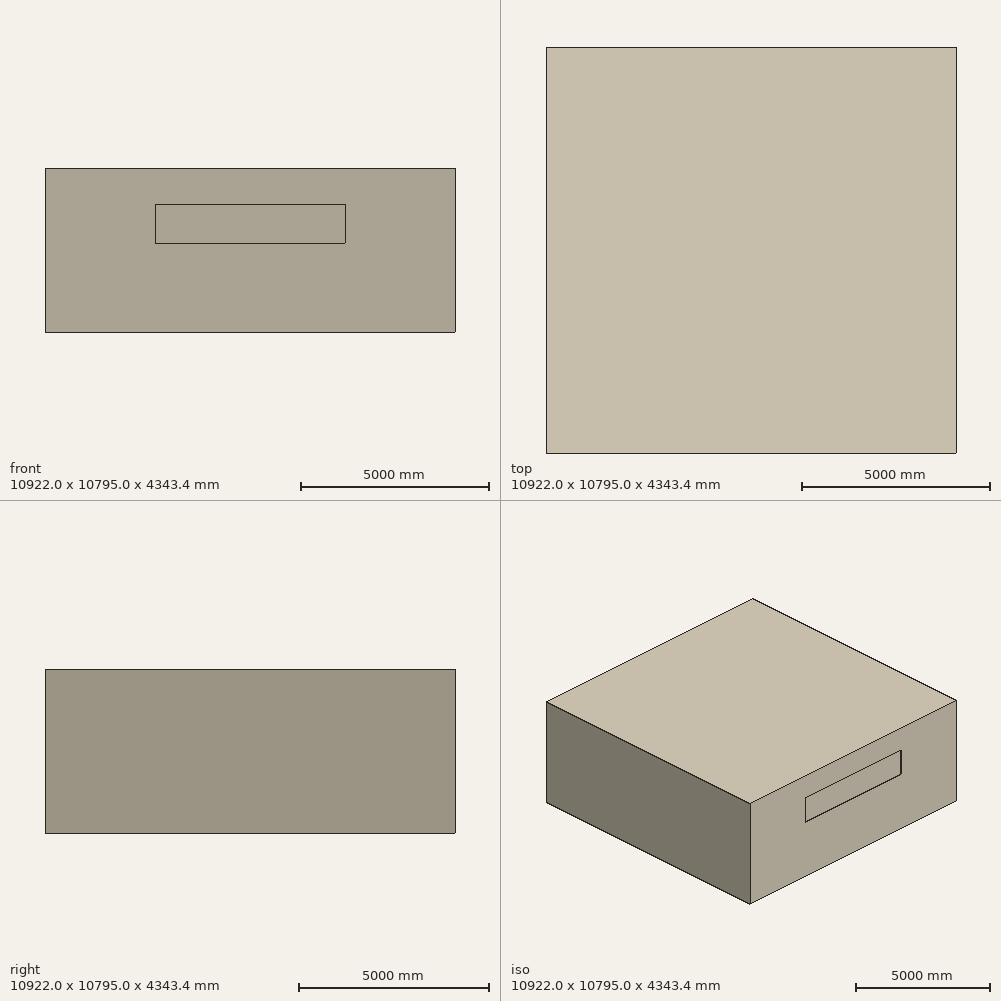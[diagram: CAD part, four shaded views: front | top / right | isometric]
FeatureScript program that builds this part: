
annotation { "Feature Type Name" : "Feature", "Feature Type Description" : "" }
export const myFeature = defineFeature(function(context is Context, id is Id, definition is map)
    precondition{}
    {
        {
            var Q0;
            Q0=qCreatedBy(makeId("Front.planeOp"),FACE);
            var sketch = newSketch(context, id + "F0", { "sketchPlane" : qUnion([Q0])});
            skLineSegment(sketch, "E0.bottom", {"start": v(-5461, -2171.7) * mm, "end": v(5461, -2171.7) * mm});
            skLineSegment(sketch, "E0.top", {"start": v(-5461, 2171.7) * mm, "end": v(5461, 2171.7) * mm});
            skLineSegment(sketch, "E0.left", {"start": v(-5461, -2171.7) * mm, "end": v(-5461, 2171.7) * mm});
            skLineSegment(sketch, "E0.right", {"start": v(5461, -2171.7) * mm, "end": v(5461, 2171.7) * mm});
            skPoint(sketch, "E0.middle", {"position": v(0, 0) * mm});
            skSolve(sketch);
        }
        {
            var Q0;
            Q0 = qSketchRegion(id + "F0", true);
            extrude(context, id + "F1", {"entities" : qUnion([Q0]), "depth" : 10795 * mm});
        }
        {
            var Q0;
            Q0=makeQuery(id+"F1.opExtrude","CAP_FACE",FACE,{"disambiguationData":[OSD([sQuery(id+"F0.wireOp",EDGE,"E0.bottom"),sQuery(id+"F0.wireOp",EDGE,"E0.top"),sQuery(id+"F0.wireOp",EDGE,"E0.left"),sQuery(id+"F0.wireOp",EDGE,"E0.right")])],"isStart":false});
            var sketch = newSketch(context, id + "F2", { "sketchPlane" : qUnion([Q0])});
            skLineSegment(sketch, "E1.bottom", {"start": v(-2535.01, 1221.87) * mm, "end": v(2535.01, 1221.87) * mm});
            skLineSegment(sketch, "E1.top", {"start": v(-2535.01, 179.2) * mm, "end": v(2535.01, 179.2) * mm});
            skLineSegment(sketch, "E1.left", {"start": v(-2535.01, 1221.87) * mm, "end": v(-2535.01, 179.2) * mm});
            skLineSegment(sketch, "E1.right", {"start": v(2535.01, 1221.87) * mm, "end": v(2535.01, 179.2) * mm});
            skPoint(sketch, "E1.middle", {"position": v(0, 700.54) * mm});
            skPoint(sketch, "E1.middle.positionSnap0", {"position": v(0, 2171.7) * mm});
            skPoint(sketch, "E1.centerSnap0", {"position": v(0, 2171.7) * mm});
            skSolve(sketch);
        }
        {
            var Q0;
            Q0 = qSketchRegion(id + "F2", true);
            extrude(context, id + "F3", {"entities" : qUnion([Q0]), "operationType" : NewBodyOperationType.REMOVE, "oppositeDirection" : true, "depth" : 25.4 * mm});
        }
    });
